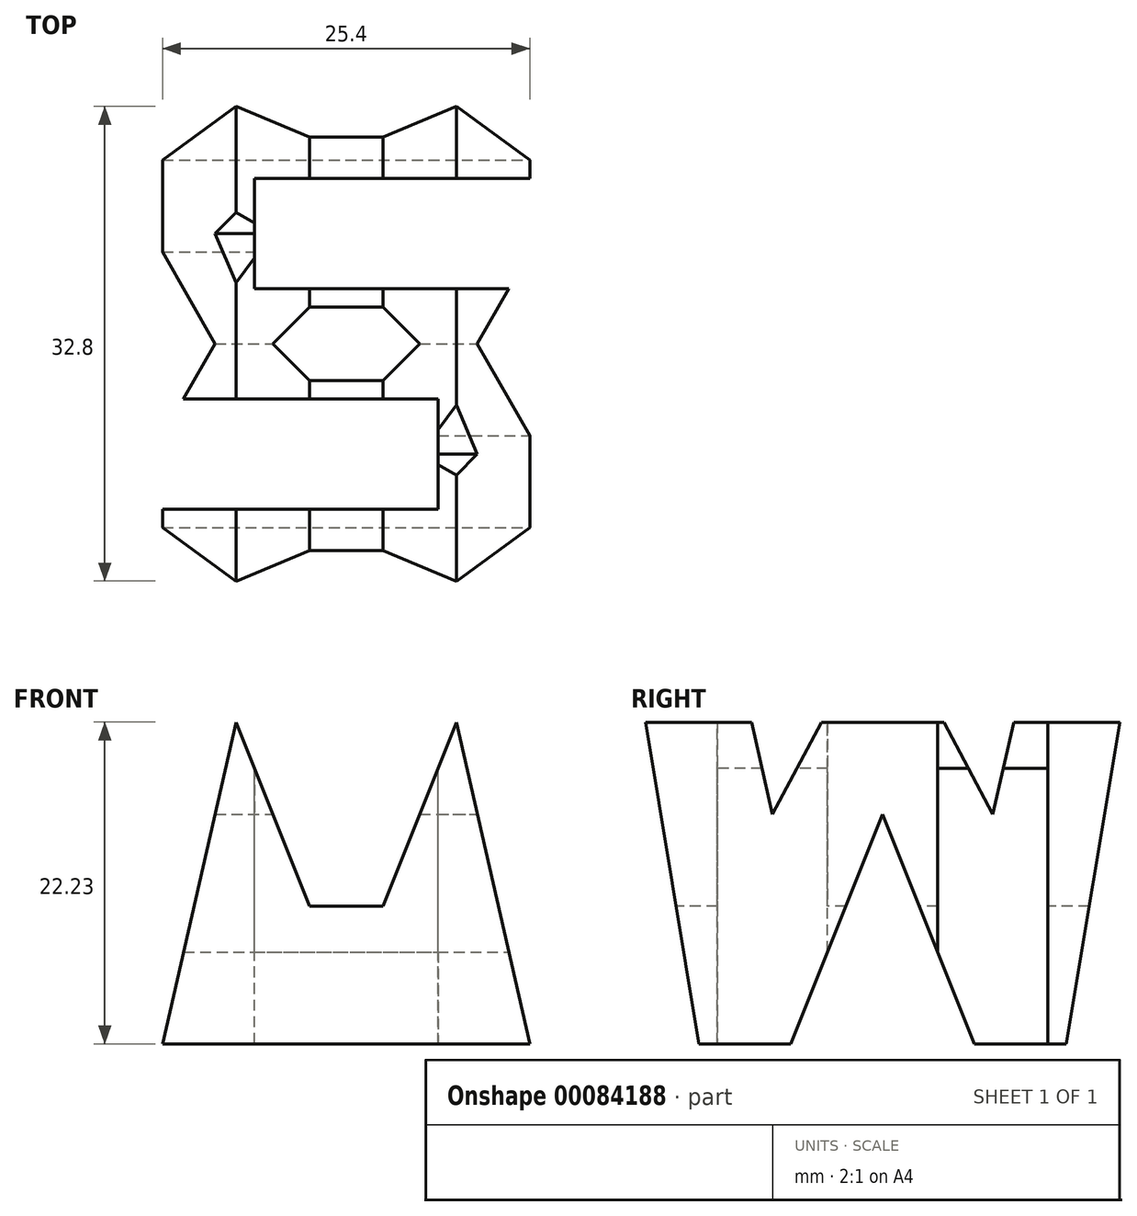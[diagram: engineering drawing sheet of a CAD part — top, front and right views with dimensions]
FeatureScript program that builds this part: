
annotation { "Feature Type Name" : "Feature", "Feature Type Description" : "" }
export const myFeature = defineFeature(function(context is Context, id is Id, definition is map)
    precondition{}
    {
        {
            var Q0;
            Q0=qCreatedBy(makeId("Front.planeOp"),FACE);
            var sketch = newSketch(context, id + "F0", { "sketchPlane" : qUnion([Q0])});
            skLineSegment(sketch, "E0", {"start": v(0, 0) * mm, "end": v(0, 38.1) * mm});
            skLineSegment(sketch, "E1", {"start": v(0, 0) * mm, "end": v(38.1, 0) * mm});
            skLineSegment(sketch, "E2", {"start": v(38.1, 0) * mm, "end": v(38.1, 38.1) * mm});
            skLineSegment(sketch, "E3", {"start": v(38.1, 38.1) * mm, "end": v(0, 38.1) * mm});
            skSolve(sketch);
        }
        {
            var Q0;
            Q0 = qSketchRegion(id + "F0", true);
            extrude(context, id + "F1", {"entities" : qUnion([Q0]), "depth" : 38.1 * mm});
        }
        {
            var Q0;
            Q0=qCreatedBy(makeId("Front.planeOp"),FACE);
            cPlane(context, id + "F2", {"entities" : qUnion([Q0]), "cplaneType" : CPlaneType.OFFSET, "offset" : 38.1 * mm, "width" : 152.4 * mm, "height" : 152.4 * mm});
        }
        {
            var Q0;
            Q0=qCreatedBy(makeId("Top.planeOp"),FACE);
            cPlane(context, id + "F3", {"entities" : qUnion([Q0]), "cplaneType" : CPlaneType.OFFSET, "offset" : 38.1 * mm, "width" : 152.4 * mm, "height" : 152.4 * mm});
        }
        {
            var Q0;
            Q0=makeQuery(id+"F1.opExtrude","SWEPT_FACE",FACE,{"disambiguationData":[OSD([sQuery(id+"F0.wireOp",EDGE,"E2")])]});
            var sketch = newSketch(context, id + "F4", { "sketchPlane" : qUnion([Q0])});
            skLineSegment(sketch, "E4", {"start": v(-38.1, 38.1) * mm, "end": v(-31.75, 0) * mm});
            skLineSegment(sketch, "E5", {"start": v(-31.75, 0) * mm, "end": v(-25.4, 0) * mm});
            skLineSegment(sketch, "E6", {"start": v(-25.4, 0) * mm, "end": v(-19.05, 15.88) * mm});
            skLineSegment(sketch, "E7", {"start": v(-19.05, 15.88) * mm, "end": v(-12.7, 0) * mm});
            skLineSegment(sketch, "E8", {"start": v(-12.7, 0) * mm, "end": v(-6.35, 0) * mm});
            skLineSegment(sketch, "E9", {"start": v(-6.35, 0) * mm, "end": v(0, 38.1) * mm});
            skLineSegment(sketch, "E10", {"start": v(0, 38.1) * mm, "end": v(-6.35, 38.1) * mm});
            skLineSegment(sketch, "E11", {"start": v(-6.35, 38.1) * mm, "end": v(-11.43, 15.88) * mm});
            skLineSegment(sketch, "E12", {"start": v(-11.43, 15.87) * mm, "end": v(-16.5, 25.4) * mm});
            skLineSegment(sketch, "E13", {"start": v(-16.5, 25.4) * mm, "end": v(-21.59, 25.4) * mm});
            skLineSegment(sketch, "E14", {"start": v(-21.59, 25.4) * mm, "end": v(-26.67, 15.88) * mm});
            skLineSegment(sketch, "E15", {"start": v(-26.67, 15.88) * mm, "end": v(-31.75, 38.1) * mm});
            skLineSegment(sketch, "E16", {"start": v(-31.75, 38.1) * mm, "end": v(-38.1, 38.1) * mm});
            skSolve(sketch);
        }
        {
            var Q0;
            {var subQ0=sQuery(id+"F4.wireOp",EDGE,"E11");Q0=makeQuery(id+"F4.imprint","IMPRINT",FACE,{"disambiguationData":[TD([[makeQuery(id+"F4.imprint","IMPRINT",EDGE,{"derivedFrom":subQ0}),-1.0]])]});}
            var Q1;
            {var subQ0=sQuery(id+"F4.wireOp",EDGE,"E4");Q1=makeQuery(id+"F4.imprint","IMPRINT",FACE,{"disambiguationData":[TD([[makeQuery(id+"F4.imprint","IMPRINT",EDGE,{"derivedFrom":subQ0}),-1.0]])]});}
            var Q2;
            {var subQ0=sQuery(id+"F4.wireOp",EDGE,"E6");Q2=makeQuery(id+"F4.imprint","IMPRINT",FACE,{"disambiguationData":[TD([[makeQuery(id+"F4.imprint","IMPRINT",EDGE,{"derivedFrom":subQ0}),-1.0]])]});}
            var Q3;
            {var subQ0=sQuery(id+"F4.wireOp",EDGE,"E9");Q3=makeQuery(id+"F4.imprint","IMPRINT",FACE,{"disambiguationData":[TD([[makeQuery(id+"F4.imprint","IMPRINT",EDGE,{"derivedFrom":subQ0}),-1.0]])]});}
            extrude(context, id + "F5", {"entities" : qUnion([Q0, Q1, Q2, Q3]), "operationType" : NewBodyOperationType.REMOVE, "oppositeDirection" : true, "depth" : 38.1 * mm});
        }
        {
            var Q0;
            Q0=qCreatedBy(id+"F2.planeOp",FACE);
            var sketch = newSketch(context, id + "F6", { "sketchPlane" : qUnion([Q0])});
            skLineSegment(sketch, "E17", {"start": v(0, 38.1) * mm, "end": v(0, 0) * mm});
            skLineSegment(sketch, "E18", {"start": v(0, 0) * mm, "end": v(38.1, 0) * mm});
            skLineSegment(sketch, "E19", {"start": v(38.1, 0) * mm, "end": v(38.1, 38.1) * mm});
            skLineSegment(sketch, "E20", {"start": v(38.1, 38.1) * mm, "end": v(0, 38.1) * mm});
            skLineSegment(sketch, "E21", {"start": v(6.35, 38.1) * mm, "end": v(0, 0) * mm});
            skLineSegment(sketch, "E22", {"start": v(0, 0) * mm, "end": v(6.35, 0) * mm});
            skLineSegment(sketch, "E23", {"start": v(6.35, 0) * mm, "end": v(11.43, 22.23) * mm});
            skLineSegment(sketch, "E24", {"start": v(11.43, 22.23) * mm, "end": v(16.51, 9.53) * mm});
            skLineSegment(sketch, "E25", {"start": v(16.51, 9.53) * mm, "end": v(21.6, 9.53) * mm});
            skLineSegment(sketch, "E26", {"start": v(21.6, 9.53) * mm, "end": v(26.67, 22.23) * mm});
            skLineSegment(sketch, "E27", {"start": v(26.67, 22.23) * mm, "end": v(31.75, 0) * mm});
            skLineSegment(sketch, "E28", {"start": v(31.75, 0) * mm, "end": v(38.1, 0) * mm});
            skLineSegment(sketch, "E29", {"start": v(38.1, 0) * mm, "end": v(31.75, 38.1) * mm});
            skLineSegment(sketch, "E30", {"start": v(31.75, 38.1) * mm, "end": v(25.4, 38.1) * mm});
            skLineSegment(sketch, "E31", {"start": v(25.4, 38.1) * mm, "end": v(19.05, 22.22) * mm});
            skLineSegment(sketch, "E32", {"start": v(19.05, 22.23) * mm, "end": v(12.7, 38.1) * mm});
            skLineSegment(sketch, "E33", {"start": v(12.7, 38.1) * mm, "end": v(6.35, 38.1) * mm});
            skSolve(sketch);
        }
        {
            var Q0;
            {var subQ0=sQuery(id+"F6.wireOp",EDGE,"E31");Q0=makeQuery(id+"F6.imprint","IMPRINT",FACE,{"disambiguationData":[TD([[makeQuery(id+"F6.imprint","IMPRINT",EDGE,{"derivedFrom":subQ0}),-1.0]])]});}
            var Q1;
            {var subQ0=sQuery(id+"F6.wireOp",EDGE,"E17");Q1=makeQuery(id+"F6.imprint","IMPRINT",FACE,{"disambiguationData":[TD([[makeQuery(id+"F6.imprint","IMPRINT",EDGE,{"derivedFrom":subQ0}),1.0]])]});}
            var Q2;
            Q2=makeQuery(id+"F6.imprint","IMPRINT",FACE,{"disambiguationData":[TD([[makeQuery(id+"F6.imprint","IMPRINT",EDGE,{"derivedFrom":sQuery(id+"F6.wireOp",EDGE,"E18")}),1.0]])]});
            var Q3;
            {var subQ0=sQuery(id+"F6.wireOp",EDGE,"E19");Q3=makeQuery(id+"F6.imprint","IMPRINT",FACE,{"disambiguationData":[TD([[makeQuery(id+"F6.imprint","IMPRINT",EDGE,{"derivedFrom":subQ0}),1.0]])]});}
            extrude(context, id + "F7", {"entities" : qUnion([Q0, Q1, Q2, Q3]), "operationType" : NewBodyOperationType.REMOVE, "oppositeDirection" : true, "depth" : 38.1 * mm});
        }
        {
            var Q0;
            Q0=qCreatedBy(id+"F3.planeOp",FACE);
            var sketch = newSketch(context, id + "F8", { "sketchPlane" : qUnion([Q0])});
            skLineSegment(sketch, "E34", {"start": v(38.1, -38.1) * mm, "end": v(38.1, 0) * mm});
            skLineSegment(sketch, "E35", {"start": v(38.1, 0) * mm, "end": v(0, 0) * mm});
            skLineSegment(sketch, "E36", {"start": v(0, 0) * mm, "end": v(0, -38.1) * mm});
            skLineSegment(sketch, "E37", {"start": v(0, -38.1) * mm, "end": v(38.1, -38.1) * mm});
            skLineSegment(sketch, "E38", {"start": v(0, -30.48) * mm, "end": v(25.4, -30.48) * mm});
            skLineSegment(sketch, "E39", {"start": v(25.4, -30.48) * mm, "end": v(25.4, -22.86) * mm});
            skLineSegment(sketch, "E40", {"start": v(25.4, -22.86) * mm, "end": v(0, -22.86) * mm});
            skLineSegment(sketch, "E41", {"start": v(38.1, -15.24) * mm, "end": v(12.7, -15.24) * mm});
            skLineSegment(sketch, "E42", {"start": v(12.7, -15.24) * mm, "end": v(12.7, -7.62) * mm});
            skLineSegment(sketch, "E43", {"start": v(12.7, -7.62) * mm, "end": v(38.1, -7.62) * mm});
            skSolve(sketch);
        }
        {
            var Q0;
            {var subQ0=sQuery(id+"F8.wireOp",EDGE,"E38");Q0=makeQuery(id+"F8.imprint","IMPRINT",FACE,{"disambiguationData":[TD([[makeQuery(id+"F8.imprint","IMPRINT",EDGE,{"derivedFrom":subQ0}),1.0]])]});}
            var Q1;
            {var subQ0=sQuery(id+"F8.wireOp",EDGE,"E41");Q1=makeQuery(id+"F8.imprint","IMPRINT",FACE,{"disambiguationData":[TD([[makeQuery(id+"F8.imprint","IMPRINT",EDGE,{"derivedFrom":subQ0}),-1.0]])]});}
            extrude(context, id + "F9", {"entities" : qUnion([Q0, Q1]), "operationType" : NewBodyOperationType.REMOVE, "oppositeDirection" : true, "depth" : 38.1 * mm});
        }
    });
